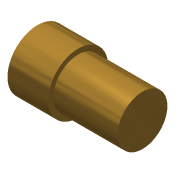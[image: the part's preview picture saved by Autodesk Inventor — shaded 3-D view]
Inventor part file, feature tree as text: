
AUTODESK INVENTOR PART (.ipt)
format: ipt  version: 2016 (Build 200138000, 138)  size: 94,208 bytes
history: native  units: in
note: dims shown in document units (in); Inventor stores cm internally (conversion verified against a paired STEP export)
features: extrude x3, sketch x3
ambient origin geometry x8: Origin, YZ Plane, XZ Plane, XY Plane, X Axis, Y Axis, Z Axis, Center Point
bodies: Solid1 (feature_tree)
feature tree (6):
  extrude  "Extrusion1"  Depth=1.36in TaperAngle=0.0deg
  extrude  "Extrusion2"  Depth=2.15in TaperAngle=0.0deg
  extrude  "Extrusion3"  Depth=0.329in
  sketch  "Sketch1"  dims[d0=2.0in d1=1.36in d2=0.0in]
  sketch  "Sketch2"  dims[d3=1.66in d4=2.15in d5=0.0in]
  sketch  "Sketch3"  dims[d7=0.75in d8=0.0in d9=0.25in d10=0.329in]
